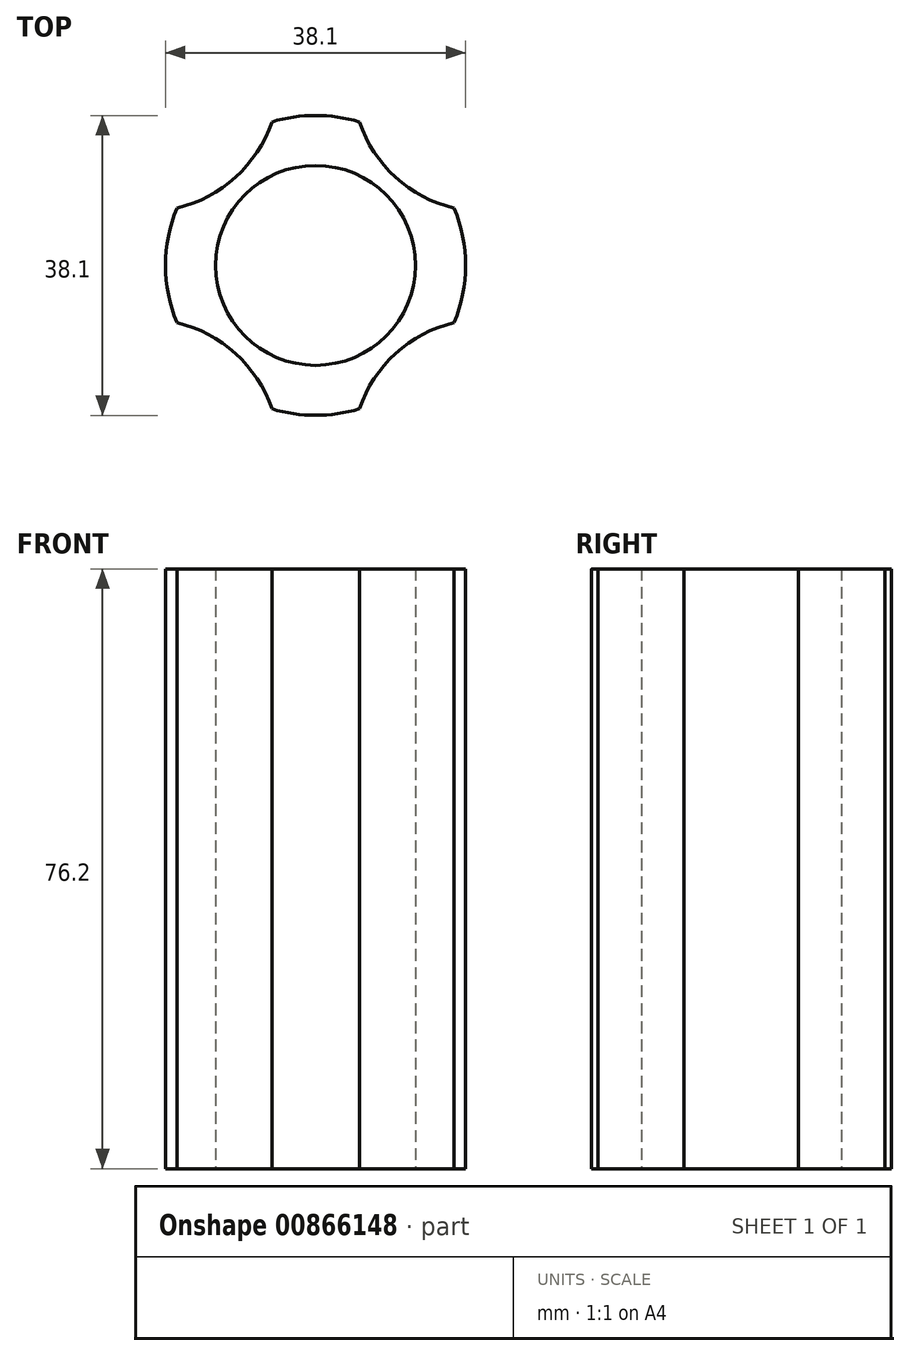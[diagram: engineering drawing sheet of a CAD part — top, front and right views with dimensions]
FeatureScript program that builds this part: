
annotation { "Feature Type Name" : "Feature", "Feature Type Description" : "" }
export const myFeature = defineFeature(function(context is Context, id is Id, definition is map)
    precondition{}
    {
        {
            var Q0;
            Q0=qCreatedBy(makeId("Top.planeOp"),FACE);
            var sketch = newSketch(context, id + "F0", { "sketchPlane" : qUnion([Q0])});
            skCircle(sketch, "E0", {"center": v(0, 0) * mm, "radius": 19.05 * mm});
            skCircle(sketch, "E1", {"center": v(0, 0) * mm, "radius": 12.7 * mm});
            skCircle(sketch, "E2", {"center": v(21.55, 23.72) * mm, "radius": 16.92 * mm});
            skCircle(sketch, "E3.MirrorC", {"center": v(-21.55, 23.72) * mm, "radius": 16.92 * mm});
            skCircle(sketch, "E4.MirrorC", {"center": v(-21.55, -23.72) * mm, "radius": 16.92 * mm});
            skCircle(sketch, "E5.MirrorC", {"center": v(21.55, -23.72) * mm, "radius": 16.92 * mm});
            skSolve(sketch);
        }
        {
            var Q0;
            Q0=makeQuery(id+"F0.imprint","IMPRINT",FACE,{"disambiguationData":[TD([[makeQuery(id+"F0.imprint","IMPRINT",EDGE,{"derivedFrom":sQuery(id+"F0.wireOp",EDGE,"E0")}),1.0]])]});
            extrude(context, id + "F1", {"entities" : qUnion([Q0]), "depth" : 76.2 * mm, "offsetDistance" : 25.4 * mm});
        }
    });
